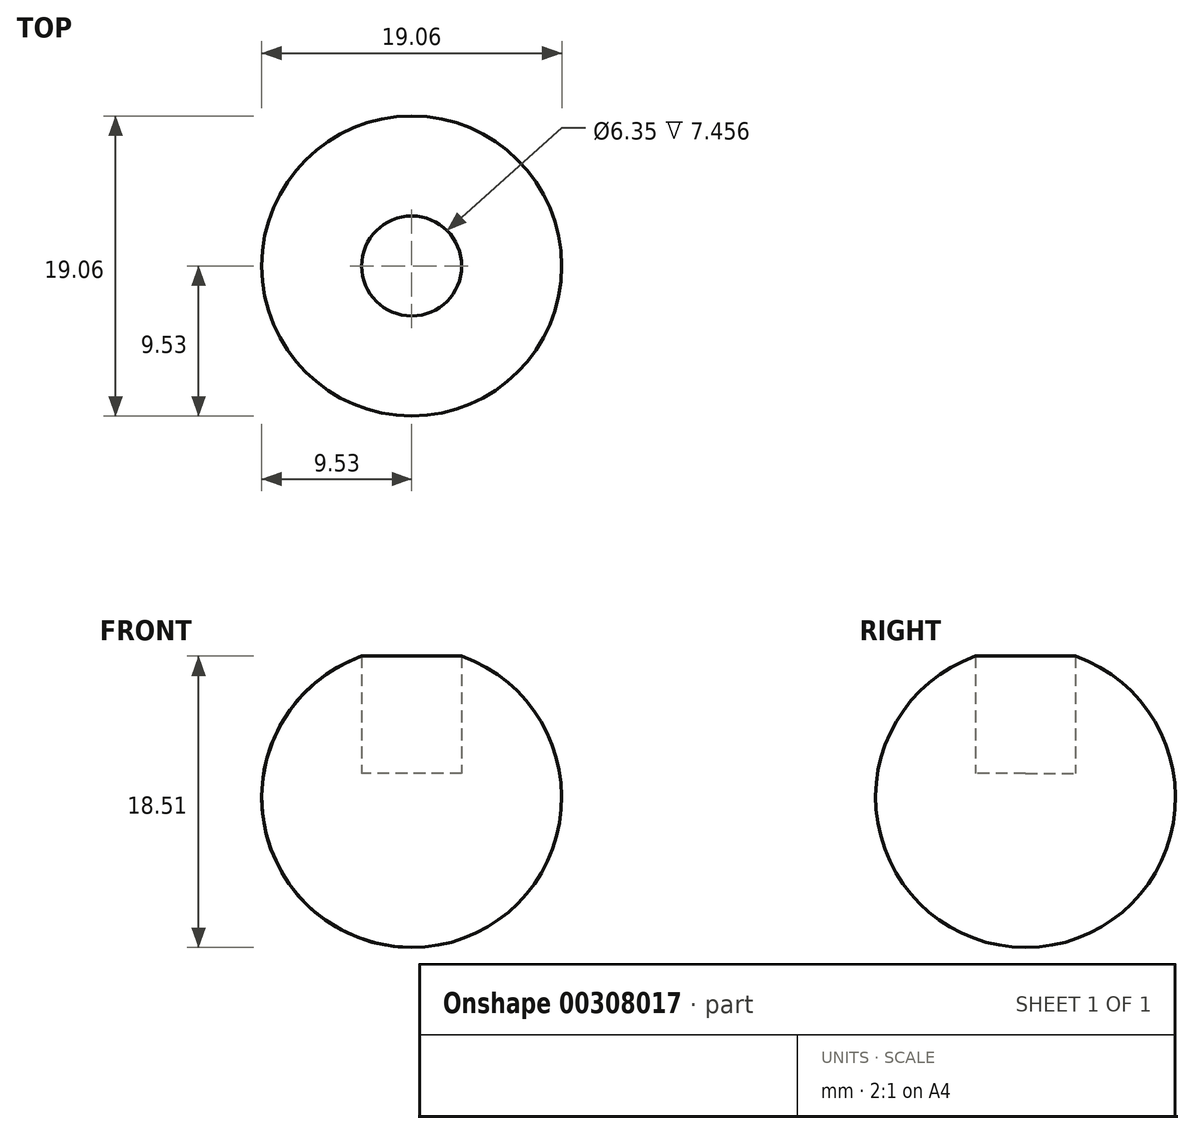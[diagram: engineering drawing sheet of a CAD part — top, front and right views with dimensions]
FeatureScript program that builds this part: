
annotation { "Feature Type Name" : "Feature", "Feature Type Description" : "" }
export const myFeature = defineFeature(function(context is Context, id is Id, definition is map)
    precondition{}
    {
        {
            var Q0;
            Q0=qCreatedBy(makeId("Front.planeOp"),FACE);
            var sketch = newSketch(context, id + "F0", { "sketchPlane" : qUnion([Q0])});
            skArc(sketch, "E0", {"start": v(0, 9.53) * mm, "mid": v(-9.53, 0) * mm, "end": v(0, -9.53) * mm});
            skLineSegment(sketch, "E1", {"start": v(0, 9.53) * mm, "end": v(0, -9.53) * mm});
            skSolve(sketch);
        }
        {
            var Q0;
            Q0=qCreatedBy(makeId("Top.planeOp"),FACE);
            var sketch = newSketch(context, id + "F1", { "sketchPlane" : qUnion([Q0])});
            skCircle(sketch, "E2", {"center": v(0, 0) * mm, "radius": 9.53 * mm});
            skSolve(sketch);
        }
        {
            var Q0;
            Q0=makeQuery(id+"F0.imprint","IMPRINT",FACE,{"disambiguationData":[TD([[makeQuery(id+"F0.imprint","IMPRINT",EDGE,{"derivedFrom":sQuery(id+"F0.wireOp",EDGE,"E0")}),1.0]])]});
            var Q1;
            Q1=sQuery(id+"F1.wireOp",EDGE,"E2");
            revolve(context, id + "F2", {"entities" : qUnion([Q0]), "axis" : qUnion([Q1]), "revolveType" : RevolveType.FULL});
        }
        {
            var Q0;
            Q0=qCreatedBy(makeId("Top.planeOp"),FACE);
            cPlane(context, id + "F3", {"entities" : qUnion([Q0]), "cplaneType" : CPlaneType.OFFSET, "offset" : 1.52 * mm, "width" : 152.4 * mm, "height" : 152.4 * mm});
        }
        {
            var Q0;
            Q0=qCreatedBy(id+"F3.planeOp",FACE);
            var sketch = newSketch(context, id + "F4", { "sketchPlane" : qUnion([Q0])});
            skCircle(sketch, "E3", {"center": v(0, 0) * mm, "radius": 3.18 * mm});
            skSolve(sketch);
        }
        {
            var Q0;
            Q0 = qSketchRegion(id + "F4", true);
            extrude(context, id + "F5", {"entities" : qUnion([Q0]), "operationType" : NewBodyOperationType.REMOVE, "depth" : 51.3 * mm});
        }
    });
